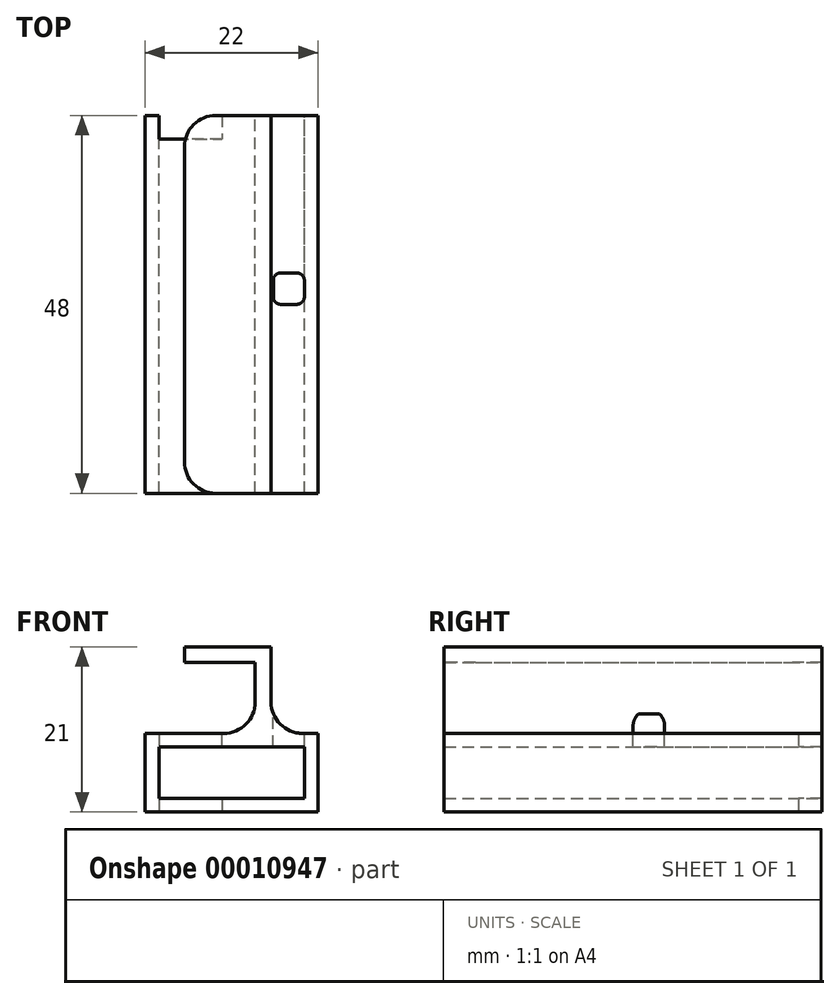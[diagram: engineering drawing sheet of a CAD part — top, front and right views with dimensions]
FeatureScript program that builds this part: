
annotation { "Feature Type Name" : "Feature", "Feature Type Description" : "" }
export const myFeature = defineFeature(function(context is Context, id is Id, definition is map)
    precondition{}
    {
        {
            var Q0;
            Q0=qCreatedBy(makeId("Front.planeOp"),FACE);
            var sketch = newSketch(context, id + "F0", { "sketchPlane" : qUnion([Q0])});
            skLineSegment(sketch, "E0", {"start": v(0, 21.02) * mm, "end": v(0, -19.81) * mm, "construction": true});
            skLineSegment(sketch, "E1.rect.bottom", {"start": v(-9.25, -3.25) * mm, "end": v(9.25, -3.25) * mm});
            skLineSegment(sketch, "E1.rect.top", {"start": v(-9.25, 3.25) * mm, "end": v(9.25, 3.25) * mm});
            skLineSegment(sketch, "E1.rect.left", {"start": v(-9.25, -3.25) * mm, "end": v(-9.25, 3.25) * mm});
            skLineSegment(sketch, "E1.rect.right", {"start": v(9.25, -3.25) * mm, "end": v(9.25, 3.25) * mm});
            skPoint(sketch, "E1.rect.middle", {"position": v(0, 0) * mm});
            skLineSegment(sketch, "E2.rect.bottom", {"start": v(11, -5) * mm, "end": v(-11, -5) * mm});
            skLineSegment(sketch, "E2.rect.top", {"start": v(11, 5) * mm, "end": v(-11, 5) * mm});
            skLineSegment(sketch, "E2.rect.left", {"start": v(11, -5) * mm, "end": v(11, 5) * mm});
            skLineSegment(sketch, "E2.rect.right", {"start": v(-11, -5) * mm, "end": v(-11, 5) * mm});
            skLineSegment(sketch, "E3", {"start": v(-9.25, -3.25) * mm, "end": v(-9.25, 5) * mm});
            skLineSegment(sketch, "E4", {"start": v(-9.25, 5) * mm, "end": v(-9.25, 7) * mm, "construction": true});
            skLineSegment(sketch, "E5", {"start": v(-9.25, 7) * mm, "end": v(-1.25, 7) * mm, "construction": true});
            skLineSegment(sketch, "E6", {"start": v(-1.25, 7) * mm, "end": v(-1.25, 5) * mm, "construction": true});
            skLineSegment(sketch, "E7", {"start": v(-1.25, 3.25) * mm, "end": v(-1.25, 5) * mm});
            skLineSegment(sketch, "E8", {"start": v(-11, 0) * mm, "end": v(-15.5, 0) * mm});
            skLineSegment(sketch, "E9.rect.left", {"start": v(-11, 4.5) * mm, "end": v(-11, -4.5) * mm});
            skPoint(sketch, "E9.rect.middle", {"position": v(-15.5, 0) * mm});
            skLineSegment(sketch, "E10", {"start": v(-1.25, -3.25) * mm, "end": v(-1.25, -5) * mm});
            skLineSegment(sketch, "E11", {"start": v(-9.25, -3.25) * mm, "end": v(-9.25, -5) * mm});
            skLineSegment(sketch, "E12", {"start": v(11, 5) * mm, "end": v(11, 7.32) * mm, "construction": true});
            skLineSegment(sketch, "E13", {"start": v(11, 7.32) * mm, "end": v(5, 7.32) * mm, "construction": true});
            skLineSegment(sketch, "E14", {"start": v(5, 5) * mm, "end": v(5, 16) * mm});
            skLineSegment(sketch, "E15", {"start": v(5, 16) * mm, "end": v(-6, 16) * mm});
            skLineSegment(sketch, "E16", {"start": v(-6, 16) * mm, "end": v(-6, 14) * mm});
            skLineSegment(sketch, "E17", {"start": v(-6, 14) * mm, "end": v(3, 14) * mm});
            skLineSegment(sketch, "E18", {"start": v(3, 14) * mm, "end": v(3, 5) * mm});
            skSolve(sketch);
        }
        {
            var Q0;
            {var subQ12=sQuery(id+"F0.wireOp",EDGE,"E1.rect.bottom");Q0=makeQuery(id+"F0.imprint","IMPRINT",FACE,{"disambiguationData":[TD([[makeQuery(id+"F0.imprint","IMPRINT",EDGE,{"derivedFrom":subQ12}),-1.0]])]});}
            var Q1;
            {var subQ0=sQuery(id+"F0.wireOp",EDGE,"E7");Q1=makeQuery(id+"F0.imprint","IMPRINT",FACE,{"disambiguationData":[TD([[makeQuery(id+"F0.imprint","IMPRINT",EDGE,{"derivedFrom":subQ0}),1.0]])]});}
            var Q2;
            {var subQ5=sQuery(id+"F0.wireOp",EDGE,"E7");Q2=makeQuery(id+"F0.imprint","IMPRINT",FACE,{"disambiguationData":[TD([[makeQuery(id+"F0.imprint","IMPRINT",EDGE,{"derivedFrom":subQ5}),-1.0]])]});}
            var Q3;
            {var subQ1=sQuery(id+"F0.wireOp",EDGE,"E14");Q3=makeQuery(id+"F0.imprint","IMPRINT",FACE,{"disambiguationData":[TD([[makeQuery(id+"F0.imprint","IMPRINT",EDGE,{"derivedFrom":subQ1}),1.0]])]});}
            var Q4;
            {var subQ8=sQuery(id+"F0.wireOp",EDGE,"E11");Q4=makeQuery(id+"F0.imprint","IMPRINT",FACE,{"disambiguationData":[TD([[makeQuery(id+"F0.imprint","IMPRINT",EDGE,{"derivedFrom":subQ8}),-1.0]])]});}
            extrude(context, id + "F1", {"entities" : qUnion([Q0, Q1, Q2, Q3, Q4]), "depth" : 45 * mm});
        }
        {
            var Q0;
            {var subQ10=sQuery(id+"F0.wireOp",EDGE,"E1.rect.right");Q0=makeQuery(id+"F0.imprint","IMPRINT",FACE,{"disambiguationData":[TD([[makeQuery(id+"F0.imprint","IMPRINT",EDGE,{"derivedFrom":subQ10}),-1.0]])]});}
            var Q1;
            {var subQ2=sQuery(id+"F0.wireOp",EDGE,"E9.rect.bottom");Q1=makeQuery(id+"F0.imprint","IMPRINT",FACE,{"disambiguationData":[TD([[makeQuery(id+"F0.imprint","IMPRINT",EDGE,{"derivedFrom":subQ2}),-1.0]])]});}
            var Q2;
            {var subQ0=sQuery(id+"F0.wireOp",EDGE,"4e665ddd-a8e6-4d16-a4a2-2a128f0cd815");Q2=makeQuery(id+"F0.imprint","IMPRINT",FACE,{"disambiguationData":[TD([[makeQuery(id+"F0.imprint","IMPRINT",EDGE,{"derivedFrom":subQ0}),1.0]])]});}
            var Q3;
            {var subQ1=sQuery(id+"F0.wireOp",EDGE,"dd019164-e9d5-4f53-80b2-175e03bbcd03");Q3=makeQuery(id+"F0.imprint","IMPRINT",FACE,{"disambiguationData":[TD([[makeQuery(id+"F0.imprint","IMPRINT",EDGE,{"derivedFrom":subQ1}),1.0]])]});}
            var Q4;
            {var subQ1=sQuery(id+"F0.wireOp",EDGE,"E9.rect.top");Q4=makeQuery(id+"F0.imprint","IMPRINT",FACE,{"disambiguationData":[TD([[makeQuery(id+"F0.imprint","IMPRINT",EDGE,{"derivedFrom":subQ1}),1.0]])]});}
            var Q5;
            Q5=makeQuery(id+"F1.opExtrude","CAP_FACE",FACE,{"disambiguationData":[OSD([sQuery(id+"F0.wireOp",EDGE,"E1.rect.bottom"),sQuery(id+"F0.wireOp",EDGE,"E1.rect.top"),sQuery(id+"F0.wireOp",EDGE,"E1.rect.right"),sQuery(id+"F0.wireOp",EDGE,"E2.rect.bottom"),sQuery(id+"F0.wireOp",EDGE,"E2.rect.top"),sQuery(id+"F0.wireOp",EDGE,"E2.rect.left"),sQuery(id+"F0.wireOp",EDGE,"E3"),sQuery(id+"F0.wireOp",EDGE,"E9.rect.bottom"),sQuery(id+"F0.wireOp",EDGE,"E9.rect.top"),sQuery(id+"F0.wireOp",EDGE,"5a380066-b404-4a13-96e5-c40744858978.rect.bottom"),sQuery(id+"F0.wireOp",EDGE,"5a380066-b404-4a13-96e5-c40744858978.rect.top"),sQuery(id+"F0.wireOp",EDGE,"5a380066-b404-4a13-96e5-c40744858978.rect.left"),sQuery(id+"F0.wireOp",EDGE,"5a380066-b404-4a13-96e5-c40744858978.rect.right"),sQuery(id+"F0.wireOp",EDGE,"4e665ddd-a8e6-4d16-a4a2-2a128f0cd815"),sQuery(id+"F0.wireOp",EDGE,"d25dc361-6c43-4e65-aefb-ce0b2837932a"),sQuery(id+"F0.wireOp",EDGE,"dd019164-e9d5-4f53-80b2-175e03bbcd03"),sQuery(id+"F0.wireOp",EDGE,"ee932de2-01f3-4a19-8076-9315cbd93f22")])],"isStart":false});
            var Q6;
            {var subQ5=sQuery(id+"F0.wireOp",EDGE,"E7");Q6=makeQuery(id+"F0.imprint","IMPRINT",FACE,{"disambiguationData":[TD([[makeQuery(id+"F0.imprint","IMPRINT",EDGE,{"derivedFrom":subQ5}),-1.0]])]});}
            var Q7;
            {var subQ0=sQuery(id+"F0.wireOp",EDGE,"E11");Q7=makeQuery(id+"F0.imprint","IMPRINT",FACE,{"disambiguationData":[TD([[makeQuery(id+"F0.imprint","IMPRINT",EDGE,{"derivedFrom":subQ0}),-1.0]])]});}
            var Q8;
            {var subQ1=sQuery(id+"F0.wireOp",EDGE,"E14");Q8=makeQuery(id+"F0.imprint","IMPRINT",FACE,{"disambiguationData":[TD([[makeQuery(id+"F0.imprint","IMPRINT",EDGE,{"derivedFrom":subQ1}),1.0]])]});}
            extrude(context, id + "F2", {"entities" : qUnion([Q0, Q1, Q2, Q3, Q4, Q5, Q6, Q7, Q8]), "operationType" : NewBodyOperationType.ADD, "oppositeDirection" : true, "depth" : 3 * mm});
        }
        {
            var Q0;
            Q0=makeQuery(id+"F1.opExtrude","SWEPT_EDGE",EDGE,{"disambiguationData":[OSD([sQuery(id+"F0.wireOp",EDGE,"E2.rect.top"),sQuery(id+"F0.wireOp",EDGE,"E18")])]});
            var Q1;
            Q1=makeQuery(id+"F1.opExtrude","CAP_EDGE",EDGE,{"disambiguationData":[OSD([sQuery(id+"F0.wireOp",EDGE,"E16")])],"isStart":true});
            var Q2;
            Q2=makeQuery(id+"F1.opExtrude","CAP_EDGE",EDGE,{"disambiguationData":[OSD([sQuery(id+"F0.wireOp",EDGE,"E16")])],"isStart":false});
            var Q3;
            Q3=makeQuery(id+"F1.opExtrude","SWEPT_EDGE",EDGE,{"disambiguationData":[OSD([sQuery(id+"F0.wireOp",EDGE,"E2.rect.top"),sQuery(id+"F0.wireOp",EDGE,"E14")])]});
            var Q4;
            {var subQ0=sQuery(id+"F0.wireOp",EDGE,"E16");Q4=makeQuery(id+"F2.opExtrude","CAP_EDGE",EDGE,{"disambiguationData":[OSD([subQ0]),TDD([makeQuery(id+"F0.imprint","IMPRINT",EDGE,{"derivedFrom":subQ0})])],"isStart":false});}
            fillet(context, id + "F3", {"entities" : qUnion([Q0, Q1, Q2, Q3, Q4]), "radius" : 4 * mm, "tangentPropagation" : true, "allowEdgeOverflow" : false});
        }
        {
            var Q0;
            {var subQ0=sQuery(id+"F0.wireOp",EDGE,"E2.rect.top");Q0=makeQuery(id+"F2.boolean.opBoolean","MERGE",FACE,{"derivedFrom":[makeQuery(id+"F1.opExtrude","SWEPT_FACE",FACE,{"disambiguationData":[OSD([subQ0])]}),makeQuery(id+"F2.opExtrude","SWEPT_FACE",FACE,{"disambiguationData":[OSD([subQ0]),TDD([makeQuery(id+"F0.imprint","IMPRINT",EDGE,{"disambiguationData":[TD([[makeQuery(id+"F0.imprint","INTERSECT",VERTEX,{"derivedFrom":[subQ0,sQuery(id+"F0.wireOp",EDGE,"E2.rect.left")]}),-1.0]])],"derivedFrom":subQ0})])]})]});}
            var sketch = newSketch(context, id + "F4", { "sketchPlane" : qUnion([Q0])});
            skLineSegment(sketch, "E19", {"start": v(11, 3) * mm, "end": v(9.25, 3) * mm, "construction": true});
            skLineSegment(sketch, "E20", {"start": v(9.25, 3) * mm, "end": v(9.25, -17) * mm, "construction": true});
            skLineSegment(sketch, "E21.bottom", {"start": v(9.25, -17) * mm, "end": v(5.25, -17) * mm});
            skLineSegment(sketch, "E21.top", {"start": v(9.25, -21) * mm, "end": v(5.25, -21) * mm});
            skLineSegment(sketch, "E21.left", {"start": v(9.25, -17) * mm, "end": v(9.25, -21) * mm});
            skLineSegment(sketch, "E21.right", {"start": v(5.25, -17) * mm, "end": v(5.25, -21) * mm});
            skSolve(sketch);
        }
        {
            var Q0;
            Q0=makeQuery(id+"F4.imprint","IMPRINT",FACE,{"disambiguationData":[TD([[makeQuery(id+"F4.imprint","IMPRINT",EDGE,{"derivedFrom":sQuery(id+"F4.wireOp",EDGE,"E21.bottom")}),1.0]])]});
            extrude(context, id + "F5", {"entities" : qUnion([Q0]), "operationType" : NewBodyOperationType.REMOVE, "oppositeDirection" : true, "depth" : 5 * mm, "symmetric" : true});
        }
        {
            var Q0;
            Q0=makeQuery(id+"F5.boolean.opBoolean","COPY",EDGE,{"derivedFrom":makeQuery(id+"F5.opExtrude","SWEPT_EDGE",EDGE,{"disambiguationData":[OSD([sQuery(id+"F4.wireOp",EDGE,"E21.top"),sQuery(id+"F4.wireOp",EDGE,"E21.left")])]})});
            var Q1;
            Q1=makeQuery(id+"F5.boolean.opBoolean","COPY",EDGE,{"derivedFrom":makeQuery(id+"F5.opExtrude","SWEPT_EDGE",EDGE,{"disambiguationData":[OSD([sQuery(id+"F4.wireOp",EDGE,"E21.bottom"),sQuery(id+"F4.wireOp",EDGE,"E21.left")])]})});
            var Q2;
            Q2=makeQuery(id+"F5.boolean.opBoolean","COPY",EDGE,{"derivedFrom":makeQuery(id+"F5.opExtrude","SWEPT_EDGE",EDGE,{"disambiguationData":[OSD([sQuery(id+"F4.wireOp",EDGE,"E21.bottom"),sQuery(id+"F4.wireOp",EDGE,"E21.right")])]})});
            var Q3;
            Q3=makeQuery(id+"F5.boolean.opBoolean","COPY",EDGE,{"derivedFrom":makeQuery(id+"F5.opExtrude","SWEPT_EDGE",EDGE,{"disambiguationData":[OSD([sQuery(id+"F4.wireOp",EDGE,"E21.top"),sQuery(id+"F4.wireOp",EDGE,"E21.right")])]})});
            fillet(context, id + "F6", {"entities" : qUnion([Q0, Q1, Q2, Q3]), "radius" : 1 * mm, "tangentPropagation" : true, "allowEdgeOverflow" : false});
        }
    });
